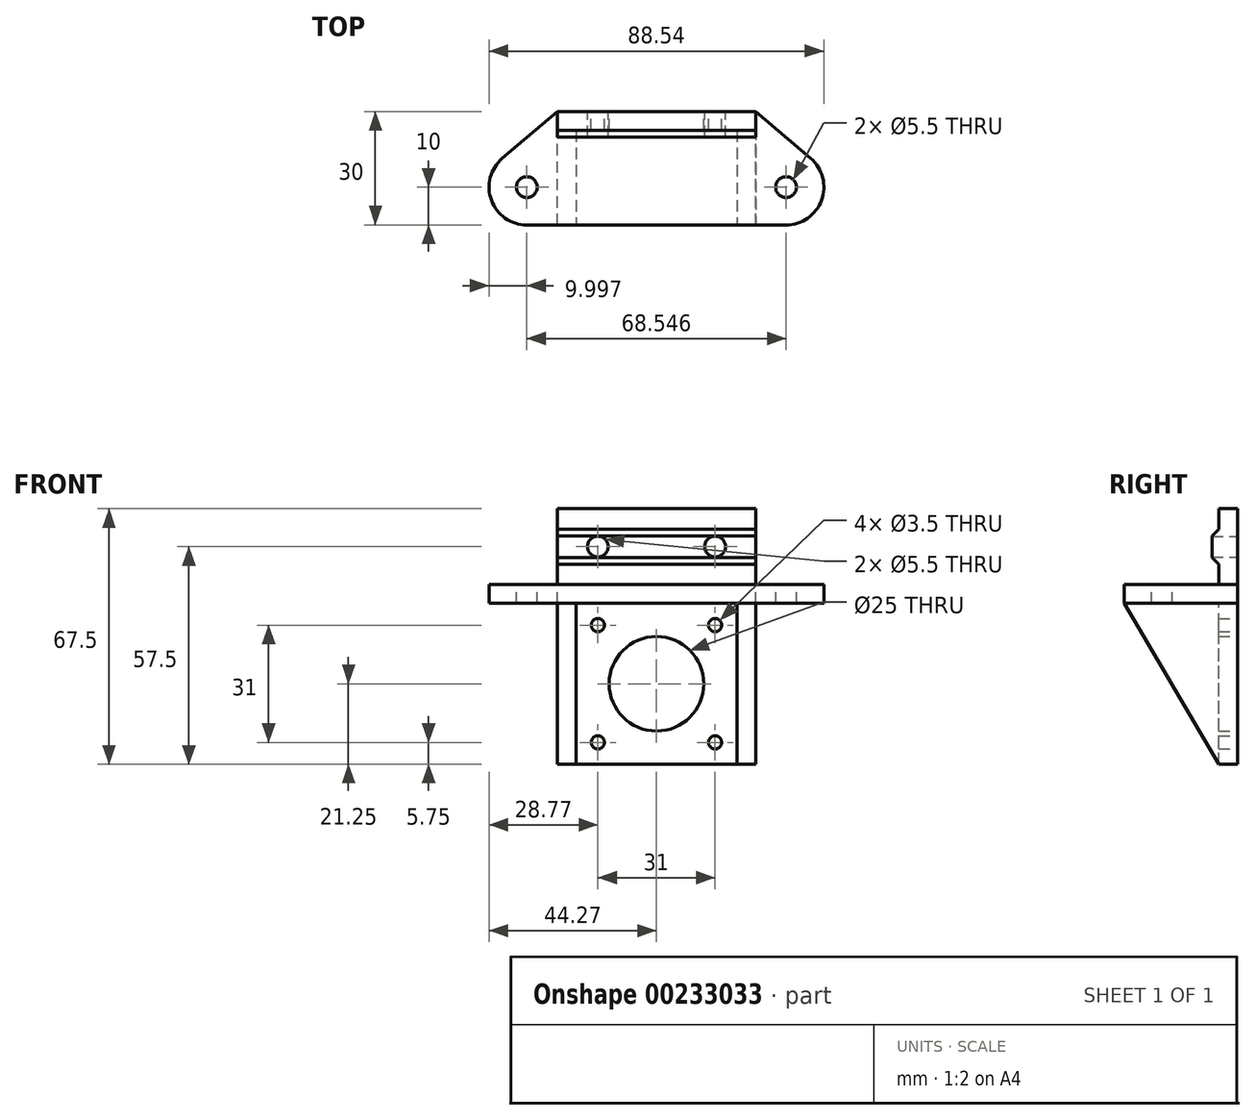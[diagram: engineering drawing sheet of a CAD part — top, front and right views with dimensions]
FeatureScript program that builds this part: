
annotation { "Feature Type Name" : "Feature", "Feature Type Description" : "" }
export const myFeature = defineFeature(function(context is Context, id is Id, definition is map)
    precondition{}
    {
        {
            var Q0;
            Q0=qCreatedBy(makeId("Front.planeOp"),FACE);
            var sketch = newSketch(context, id + "F0", { "sketchPlane" : qUnion([Q0])});
            skLineSegment(sketch, "E0.bottom", {"start": v(0, 0) * mm, "end": v(52.5, 0) * mm});
            skLineSegment(sketch, "E0.top", {"start": v(0, 47.5) * mm, "end": v(52.5, 47.5) * mm});
            skLineSegment(sketch, "E0.left", {"start": v(0, 0) * mm, "end": v(0, 47.5) * mm});
            skLineSegment(sketch, "E0.right", {"start": v(52.5, 0) * mm, "end": v(52.5, 47.5) * mm});
            skCircle(sketch, "E1", {"center": v(10.75, 5.75) * mm, "radius": 1.75 * mm});
            skCircle(sketch, "E2", {"center": v(41.75, 5.75) * mm, "radius": 1.75 * mm});
            skCircle(sketch, "E3", {"center": v(41.75, 36.75) * mm, "radius": 1.75 * mm});
            skCircle(sketch, "E4", {"center": v(10.75, 36.75) * mm, "radius": 1.75 * mm});
            skCircle(sketch, "E5", {"center": v(26.25, 21.25) * mm, "radius": 12.5 * mm});
            skPoint(sketch, "E5.centerSnap0", {"position": v(26.25, 0) * mm});
            skSolve(sketch);
        }
        {
            var Q0;
            Q0 = qSketchRegion(id + "F0", true);
            extrude(context, id + "F1", {"entities" : qUnion([Q0]), "depth" : 5 * mm});
        }
        {
            var Q0;
            Q0=makeQuery(id+"F1.opExtrude","CAP_FACE",FACE,{"disambiguationData":[OSD([sQuery(id+"F0.wireOp",EDGE,"E0.bottom"),sQuery(id+"F0.wireOp",EDGE,"E0.top"),sQuery(id+"F0.wireOp",EDGE,"E0.left"),sQuery(id+"F0.wireOp",EDGE,"E0.right"),sQuery(id+"F0.wireOp",EDGE,"E1"),sQuery(id+"F0.wireOp",EDGE,"E2"),sQuery(id+"F0.wireOp",EDGE,"E3"),sQuery(id+"F0.wireOp",EDGE,"E4")])],"isStart":false});
            var sketch = newSketch(context, id + "F2", { "sketchPlane" : qUnion([Q0])});
            skLineSegment(sketch, "E6.0", {"start": v(0, 0) * mm, "end": v(0, 47.5) * mm});
            skLineSegment(sketch, "E7.0", {"start": v(0, 47.5) * mm, "end": v(52.5, 47.5) * mm});
            skLineSegment(sketch, "E8.0", {"start": v(52.5, 0) * mm, "end": v(52.5, 47.5) * mm});
            skLineSegment(sketch, "E9.0", {"start": v(0, 0) * mm, "end": v(5, 0) * mm});
            skLineSegment(sketch, "E10.0", {"start": v(47.5, 0) * mm, "end": v(47.5, 42.5) * mm});
            skLineSegment(sketch, "E10.1", {"start": v(5, 42.5) * mm, "end": v(47.5, 42.5) * mm});
            skLineSegment(sketch, "E10.2", {"start": v(5, 0) * mm, "end": v(5, 42.5) * mm});
            skLineSegment(sketch, "E11.trimOffspring", {"start": v(47.5, 0) * mm, "end": v(52.5, 0) * mm});
            skSolve(sketch);
        }
        {
            var Q0;
            Q0 = qSketchRegion(id + "F2", true);
            extrude(context, id + "F3", {"entities" : qUnion([Q0]), "operationType" : NewBodyOperationType.ADD, "depth" : 25 * mm});
        }
        {
            var Q0;
            Q0=makeQuery(id+"F3.boolean.opBoolean","MERGE",FACE,{"derivedFrom":[makeQuery(id+"F1.opExtrude","SWEPT_FACE",FACE,{"disambiguationData":[OSD([sQuery(id+"F0.wireOp",EDGE,"E0.top")])]}),makeQuery(id+"F3.opExtrude","SWEPT_FACE",FACE,{"disambiguationData":[OSD([sQuery(id+"F2.wireOp",EDGE,"E7.0")])]})]});
            var sketch = newSketch(context, id + "F4", { "sketchPlane" : qUnion([Q0])});
            skLineSegment(sketch, "E12.bottom", {"start": v(0, 0) * mm, "end": v(52.5, 0) * mm});
            skLineSegment(sketch, "E12.top", {"start": v(0, -5) * mm, "end": v(52.5, -5) * mm});
            skLineSegment(sketch, "E12.left", {"start": v(0, 0) * mm, "end": v(0, -5) * mm});
            skLineSegment(sketch, "E12.right", {"start": v(52.5, 0) * mm, "end": v(52.5, -5) * mm});
            skSolve(sketch);
        }
        {
            var Q0;
            Q0 = qSketchRegion(id + "F4", true);
            extrude(context, id + "F5", {"entities" : qUnion([Q0]), "operationType" : NewBodyOperationType.ADD, "depth" : 20 * mm});
        }
        {
            var Q0;
            Q0=makeQuery(id+"F3.boolean.opBoolean","MERGE",FACE,{"derivedFrom":[makeQuery(id+"F1.opExtrude","SWEPT_FACE",FACE,{"disambiguationData":[OSD([sQuery(id+"F0.wireOp",EDGE,"E0.top")])]}),makeQuery(id+"F3.opExtrude","SWEPT_FACE",FACE,{"disambiguationData":[OSD([sQuery(id+"F2.wireOp",EDGE,"E7.0")])]})]});
            var sketch = newSketch(context, id + "F6", { "sketchPlane" : qUnion([Q0])});
            skCircle(sketch, "E13", {"center": v(-8.02, -20) * mm, "radius": 2.75 * mm});
            skArc(sketch, "E14", {"start": v(-14.52, -12.4) * mm, "mid": v(-17.4, -23.46) * mm, "end": v(-8.02, -30) * mm});
            skLineSegment(sketch, "E15.top", {"start": v(-8.02, -30) * mm, "end": v(0, -30) * mm});
            skLineSegment(sketch, "E15.left", {"start": v(-8.02, -17.25) * mm, "end": v(-8.02, -22.75) * mm});
            skLineSegment(sketch, "E16", {"start": v(0, 0) * mm, "end": v(-14.52, -12.4) * mm});
            skLineSegment(sketch, "E17", {"start": v(0, 0) * mm, "end": v(0, -30) * mm});
            skLineSegment(sketch, "E18", {"start": v(26.25, -30) * mm, "end": v(26.25, 0) * mm, "construction": true});
            skPoint(sketch, "E18.endSnap0", {"position": v(26.25, -5) * mm});
            skLineSegment(sketch, "E19.MirrorCS", {"start": v(60.52, -17.25) * mm, "end": v(60.52, -22.75) * mm});
            skArc(sketch, "E20.MirrorCS", {"start": v(67.02, -12.4) * mm, "mid": v(69.9, -23.46) * mm, "end": v(60.52, -30) * mm});
            skLineSegment(sketch, "E21.MirrorCS", {"start": v(60.52, -30) * mm, "end": v(52.5, -30) * mm});
            skLineSegment(sketch, "E22.MirrorCS", {"start": v(52.5, 0) * mm, "end": v(52.5, -30) * mm});
            skLineSegment(sketch, "E23.MirrorCS", {"start": v(52.5, 0) * mm, "end": v(67.02, -12.4) * mm});
            skCircle(sketch, "E24.MirrorC", {"center": v(60.52, -20) * mm, "radius": 2.75 * mm});
            skSolve(sketch);
        }
        {
            var Q0;
            Q0 = qSketchRegion(id + "F6", true);
            extrude(context, id + "F7", {"entities" : qUnion([Q0]), "operationType" : NewBodyOperationType.ADD, "oppositeDirection" : true, "depth" : 5 * mm});
        }
        {
            var Q0;
            {var subQ1=sQuery(id+"F0.wireOp",EDGE,"E0.top");var subQ3=sQuery(id+"F0.wireOp",EDGE,"E0.right");var subQ4=sQuery(id+"F4.wireOp",EDGE,"E12.right");Q0=makeQuery(id+"F7.boolean.opBoolean","SPLIT",FACE,{"disambiguationData":[TD([makeQuery(id+"F1.opExtrude","SWEPT_FACE",FACE,{"disambiguationData":[OSD([subQ1])]})])],"derivedFrom":makeQuery(id+"F5.boolean.opBoolean","MERGE",FACE,{"derivedFrom":[makeQuery(id+"F3.boolean.opBoolean","MERGE",FACE,{"derivedFrom":[makeQuery(id+"F1.opExtrude","SWEPT_FACE",FACE,{"disambiguationData":[OSD([subQ3])]}),makeQuery(id+"F3.opExtrude","SWEPT_FACE",FACE,{"disambiguationData":[OSD([sQuery(id+"F2.wireOp",EDGE,"E8.0")])]})]}),makeQuery(id+"F5.opExtrude","SWEPT_FACE",FACE,{"disambiguationData":[OSD([subQ4])]})]})});}
            var sketch = newSketch(context, id + "F8", { "sketchPlane" : qUnion([Q0])});
            skLineSegment(sketch, "E25", {"start": v(-5, 52.87) * mm, "end": v(-6.79, 54.66) * mm});
            skLineSegment(sketch, "E26", {"start": v(-6.79, 54.66) * mm, "end": v(-6.79, 60.34) * mm});
            skLineSegment(sketch, "E27", {"start": v(-6.79, 60.34) * mm, "end": v(-5, 62.12) * mm});
            skLineSegment(sketch, "E28", {"start": v(-5, 62.12) * mm, "end": v(-5, 52.87) * mm});
            skSolve(sketch);
        }
        {
            var Q0;
            Q0 = qSketchRegion(id + "F8", true);
            var Q1;
            {var subQ1=sQuery(id+"F0.wireOp",EDGE,"E0.top");var subQ2=sQuery(id+"F0.wireOp",EDGE,"E0.left");var subQ4=sQuery(id+"F4.wireOp",EDGE,"E12.left");Q1=makeQuery(id+"F7.boolean.opBoolean","SPLIT",FACE,{"disambiguationData":[TD([makeQuery(id+"F1.opExtrude","SWEPT_FACE",FACE,{"disambiguationData":[OSD([subQ1])]})])],"derivedFrom":makeQuery(id+"F5.boolean.opBoolean","MERGE",FACE,{"derivedFrom":[makeQuery(id+"F3.boolean.opBoolean","MERGE",FACE,{"derivedFrom":[makeQuery(id+"F1.opExtrude","SWEPT_FACE",FACE,{"disambiguationData":[OSD([subQ2])]}),makeQuery(id+"F3.opExtrude","SWEPT_FACE",FACE,{"disambiguationData":[OSD([sQuery(id+"F2.wireOp",EDGE,"E6.0")])]})]}),makeQuery(id+"F5.opExtrude","SWEPT_FACE",FACE,{"disambiguationData":[OSD([subQ4])]})]})});}
            extrude(context, id + "F9", {"entities" : qUnion([Q0]), "operationType" : NewBodyOperationType.ADD, "endBound" : BoundingType.UP_TO_SURFACE, "oppositeDirection" : true, "endBoundEntityFace" : qUnion([Q1]), "depth" : 25 * mm});
        }
        {
            var Q0;
            Q0=makeQuery(id+"F5.boolean.opBoolean","MERGE",FACE,{"derivedFrom":[makeQuery(id+"F1.opExtrude","CAP_FACE",FACE,{"disambiguationData":[OSD([sQuery(id+"F0.wireOp",EDGE,"E0.bottom"),sQuery(id+"F0.wireOp",EDGE,"E0.top"),sQuery(id+"F0.wireOp",EDGE,"E0.left"),sQuery(id+"F0.wireOp",EDGE,"E0.right"),sQuery(id+"F0.wireOp",EDGE,"E1"),sQuery(id+"F0.wireOp",EDGE,"E2"),sQuery(id+"F0.wireOp",EDGE,"E3"),sQuery(id+"F0.wireOp",EDGE,"E4")])],"isStart":true}),makeQuery(id+"F5.opExtrude","SWEPT_FACE",FACE,{"disambiguationData":[OSD([sQuery(id+"F4.wireOp",EDGE,"E12.bottom")])]})]});
            var sketch = newSketch(context, id + "F10", { "sketchPlane" : qUnion([Q0])});
            skCircle(sketch, "E29", {"center": v(-41.75, 57.5) * mm, "radius": 2.75 * mm});
            skCircle(sketch, "E30", {"center": v(-10.75, 57.5) * mm, "radius": 2.75 * mm});
            skSolve(sketch);
        }
        {
            var Q0;
            Q0 = qSketchRegion(id + "F10", true);
            extrude(context, id + "F11", {"entities" : qUnion([Q0]), "operationType" : NewBodyOperationType.REMOVE, "endBound" : BoundingType.THROUGH_ALL, "oppositeDirection" : true, "depth" : 25 * mm});
        }
        {
            var Q0;
            {var subQ1=sQuery(id+"F0.wireOp",EDGE,"E0.right");var subQ2=sQuery(id+"F0.wireOp",EDGE,"E0.bottom");var subQ5=sQuery(id+"F2.wireOp",EDGE,"E8.0");Q0=makeQuery(id+"F7.boolean.opBoolean","SPLIT",FACE,{"disambiguationData":[TD([makeQuery(id+"F1.opExtrude","SWEPT_FACE",FACE,{"disambiguationData":[OSD([subQ2])]})])],"derivedFrom":makeQuery(id+"F5.boolean.opBoolean","MERGE",FACE,{"derivedFrom":[makeQuery(id+"F3.boolean.opBoolean","MERGE",FACE,{"derivedFrom":[makeQuery(id+"F1.opExtrude","SWEPT_FACE",FACE,{"disambiguationData":[OSD([subQ1])]}),makeQuery(id+"F3.opExtrude","SWEPT_FACE",FACE,{"disambiguationData":[OSD([subQ5])]})]}),makeQuery(id+"F5.opExtrude","SWEPT_FACE",FACE,{"disambiguationData":[OSD([sQuery(id+"F4.wireOp",EDGE,"E12.right")])]})]})});}
            var sketch = newSketch(context, id + "F12", { "sketchPlane" : qUnion([Q0])});
            skLineSegment(sketch, "E31.0.1", {"start": v(-5, 42.5) * mm, "end": v(-30, 42.5) * mm});
            skLineSegment(sketch, "E32", {"start": v(-30, 42.5) * mm, "end": v(-5, 0) * mm});
            skLineSegment(sketch, "E33", {"start": v(-30, 42.5) * mm, "end": v(-30, 0) * mm});
            skLineSegment(sketch, "E34", {"start": v(-30, 0) * mm, "end": v(-5, 0) * mm});
            skSolve(sketch);
        }
        {
            var Q0;
            Q0 = qSketchRegion(id + "F12", true);
            var Q1;
            {var subQ1=sQuery(id+"F0.wireOp",EDGE,"E0.left");var subQ2=sQuery(id+"F0.wireOp",EDGE,"E0.bottom");var subQ5=sQuery(id+"F2.wireOp",EDGE,"E6.0");Q1=makeQuery(id+"F7.boolean.opBoolean","SPLIT",FACE,{"disambiguationData":[TD([makeQuery(id+"F1.opExtrude","SWEPT_FACE",FACE,{"disambiguationData":[OSD([subQ2])]})])],"derivedFrom":makeQuery(id+"F5.boolean.opBoolean","MERGE",FACE,{"derivedFrom":[makeQuery(id+"F3.boolean.opBoolean","MERGE",FACE,{"derivedFrom":[makeQuery(id+"F1.opExtrude","SWEPT_FACE",FACE,{"disambiguationData":[OSD([subQ1])]}),makeQuery(id+"F3.opExtrude","SWEPT_FACE",FACE,{"disambiguationData":[OSD([subQ5])]})]}),makeQuery(id+"F5.opExtrude","SWEPT_FACE",FACE,{"disambiguationData":[OSD([sQuery(id+"F4.wireOp",EDGE,"E12.left")])]})]})});}
            extrude(context, id + "F13", {"entities" : qUnion([Q0]), "operationType" : NewBodyOperationType.REMOVE, "endBound" : BoundingType.UP_TO_SURFACE, "oppositeDirection" : true, "endBoundEntityFace" : qUnion([Q1]), "depth" : 25 * mm});
        }
    });
